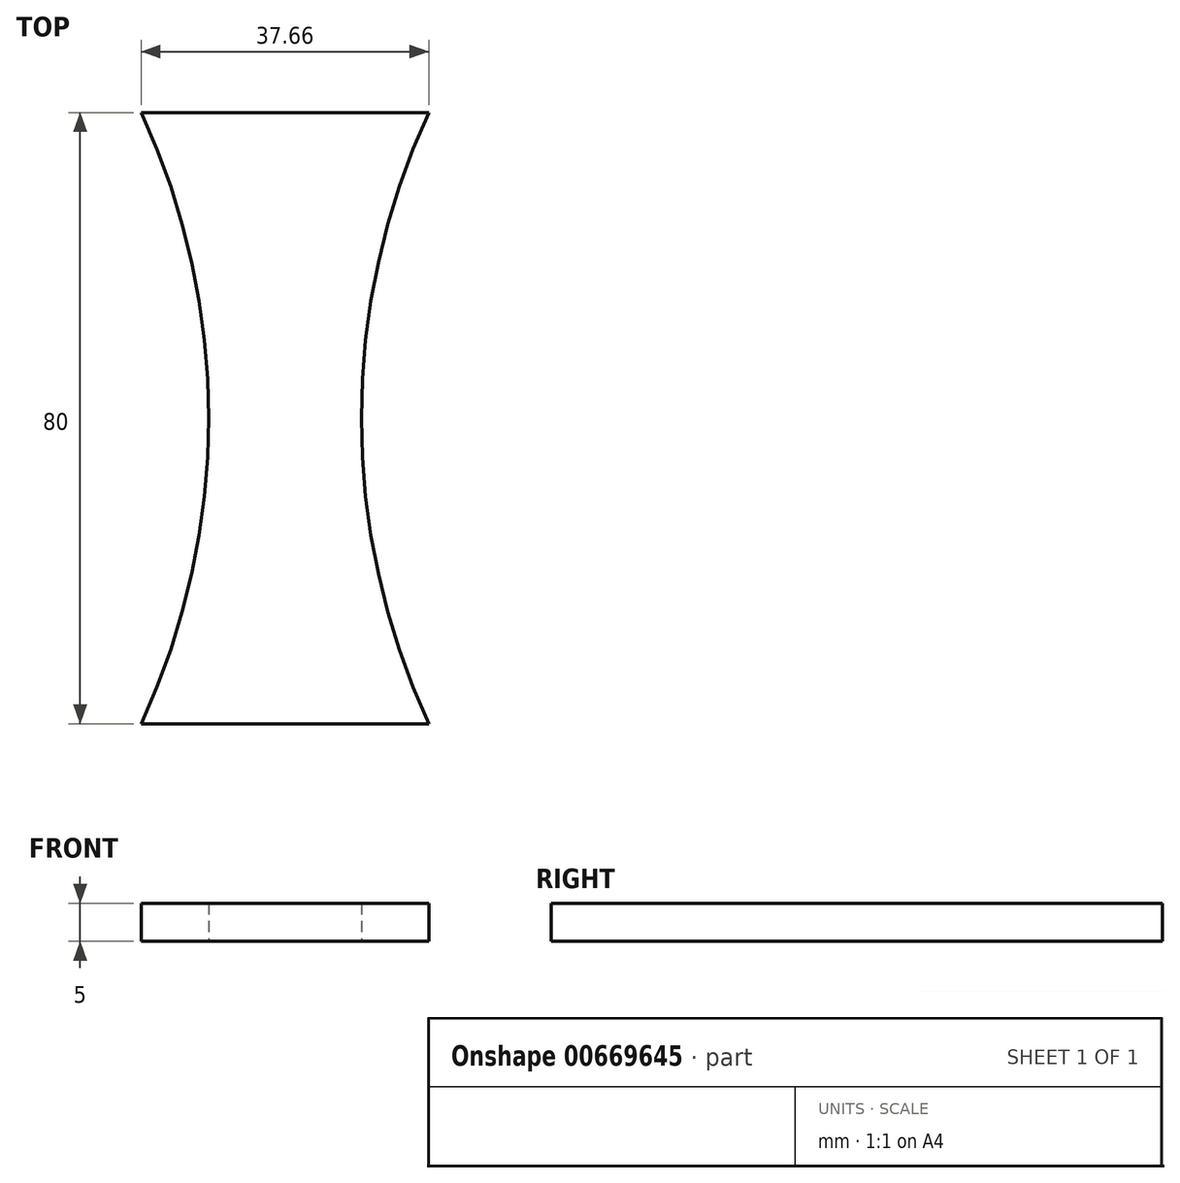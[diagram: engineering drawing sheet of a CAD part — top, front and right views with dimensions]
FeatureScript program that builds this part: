
annotation { "Feature Type Name" : "Feature", "Feature Type Description" : "" }
export const myFeature = defineFeature(function(context is Context, id is Id, definition is map)
    precondition{}
    {
        {
            var Q0;
            Q0=qCreatedBy(makeId("Top.planeOp"),FACE);
            var sketch = newSketch(context, id + "F0", { "sketchPlane" : qUnion([Q0])});
            skArc(sketch, "E0", {"start": v(-18.83, -40) * mm, "mid": v(-10, 0) * mm, "end": v(-18.83, 40) * mm});
            skArc(sketch, "E1", {"start": v(18.83, 40) * mm, "mid": v(10, 0) * mm, "end": v(18.83, -40) * mm});
            skLineSegment(sketch, "E2", {"start": v(-18.83, 40) * mm, "end": v(18.83, 40) * mm});
            skLineSegment(sketch, "E3", {"start": v(18.83, -40) * mm, "end": v(-18.83, -40) * mm});
            skLineSegment(sketch, "E4", {"start": v(0, 40) * mm, "end": v(0, -40) * mm, "construction": true});
            skSolve(sketch);
        }
        {
            var Q0;
            Q0=makeQuery(id+"F0.imprint","IMPRINT",FACE,{"disambiguationData":[TD([[makeQuery(id+"F0.imprint","IMPRINT",EDGE,{"derivedFrom":sQuery(id+"F0.wireOp",EDGE,"E0")}),-1.0]])]});
            extrude(context, id + "F1", {"entities" : qUnion([Q0]), "depth" : 5 * mm, "offsetDistance" : 25 * mm});
        }
    });
